# Revit family: LC Duplex 12 fibras
name_source: partatom
category: Installations électriques
units: mm (PartAtom-declared; Revit-internal decimal feet)

## family parameters
Basée sur le plan de construction = Non
Conserver l'orientation des annotations = Non
Cote de connecteur circulaire = Utiliser le diamètre
Couper avec des vides une fois chargée = Non
Partagée = Non
Point de calcul de pièce = Non
Toujours verticalement = Oui
Type d'élément = Normal

## types (4) — shared parameters
Altura = 23 mm  [stored 0.0754593 ft]
Altura de la apertura = 6.5 mm
Altura de los conectores = 10 mm  [stored 0.0328084 ft]
Anchura (mm) = 108.8 mm  [stored 0.356955 ft]
Anchura de la apertura = 6 mm  [stored 0.019685 ft]
Anchura de los conectores = 13.5 mm  [stored 0.0442913 ft]
Clasificación ETIM = EC001130
Color = IDS_NOIR
E-catalogo enlace = https://www.legrand.fr
Función = Paneles de interconexión con optical conector Legrand
IK = IK04
IP = IP20
Numero RAL = 9017
Número de conectores = 12
Profundidad = 38.4 mm  [stored 0.125984 ft]
Temperatura de almacenamiento = -10°C à 60°C
Temperatura operativa = -10°C à 60°C
zero-valued in all types: Elévation par défaut

## per-type parameters (varying)
| type | Color de los conectores | EAN | Formulación BIM | Número de pieza Legrand | Tipo de conector externo | Tipo de conector interno | Tipo de la fibra óptica |
| Panel de adaptadores LC Duplex 12 fibras monomodal | IDS_BLEU | 3414970961730 | Panel de adaptadores LC Duplex 12 fibras monomodal | 032114 | LC_DUPLEX | LC_DUPLEX | unimodal |
| Panel de adaptadores LC APC 12 fibras monomodal | IDS_CYAN | 3414970961778 | Panel de adaptadores LC APC 12 fibras monomodal | 032116 | LC-DUPLEX | LC-DUPLEX | unimodal |
| Panel de adaptadores LC Duplex 12 fibras multimodal | IDS_JAUNE | 3414970961877 | Panel de adaptadores LC Duplex 12 fibras multimodal | 032124 | LC_DUPLEX | LC_DUPLEX | Mutlimodal |
| Panel de adaptadores LC Duplex(AQUA)_POUR_12_FIBRES_MULTIMODE | IDS_CYAN | 3414971400313 | Panel de adaptadores LC Duplex aqua 12 fibras multimodal | 032137 | LC_DUPLEX | LC_DUPLEX | Mutlimodal |

note: [stored X ft] marks values corroborated as IEEE doubles in the binary element streams (Revit-internal decimal feet)
